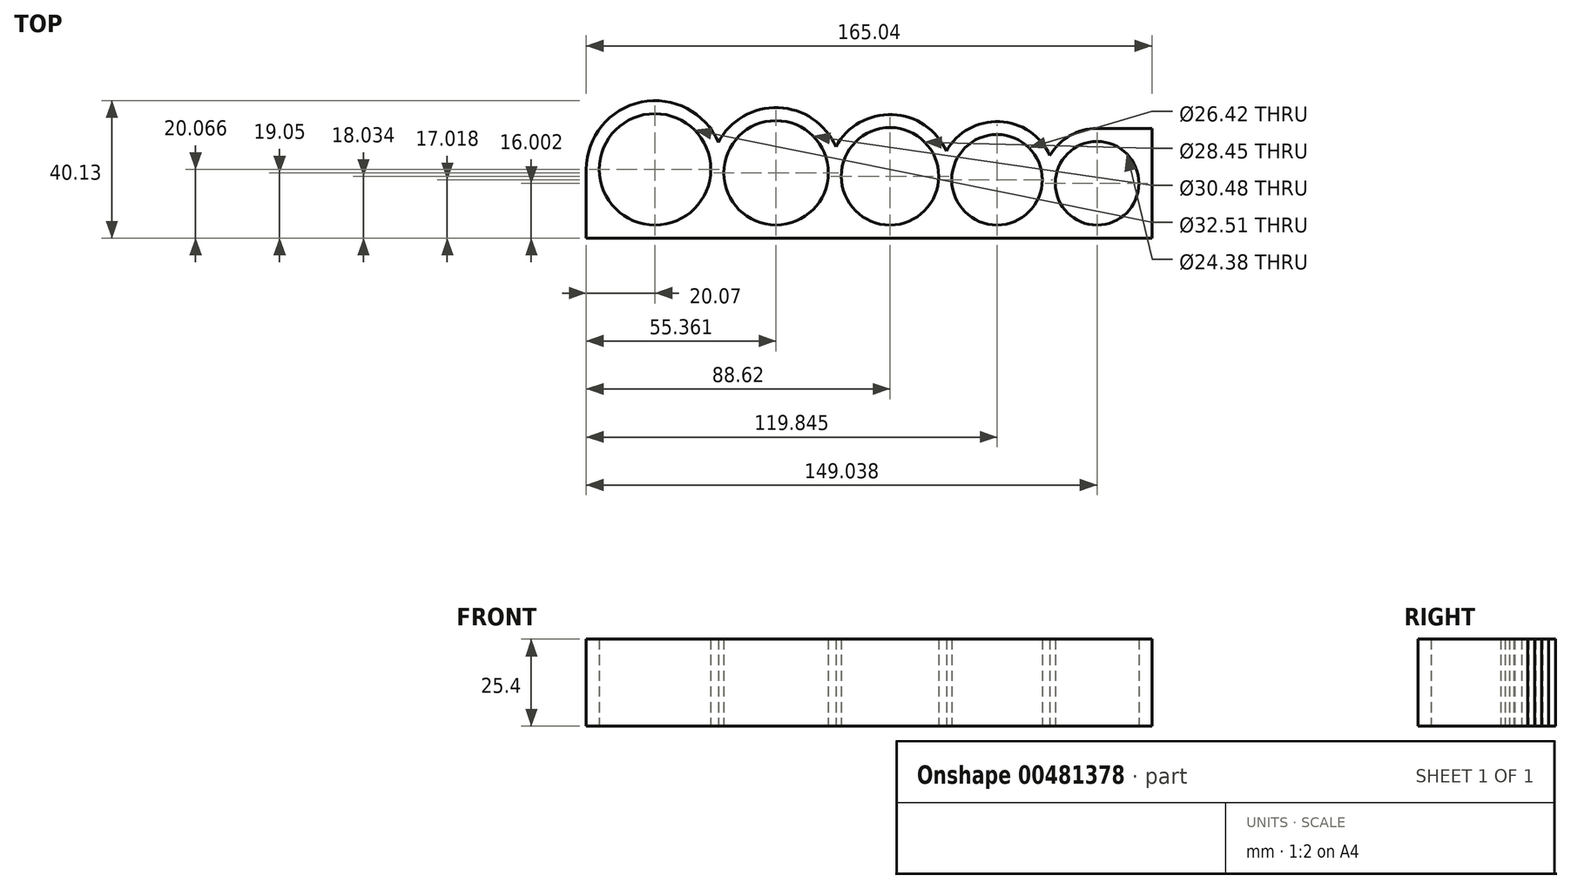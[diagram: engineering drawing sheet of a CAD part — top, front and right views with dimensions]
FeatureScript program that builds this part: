
annotation { "Feature Type Name" : "Feature", "Feature Type Description" : "" }
export const myFeature = defineFeature(function(context is Context, id is Id, definition is map)
    precondition{}
    {
        {
            var Q0;
            Q0=qCreatedBy(makeId("Top.planeOp"),FACE);
            var sketch = newSketch(context, id + "F0", { "sketchPlane" : qUnion([Q0])});
            skCircle(sketch, "E0", {"center": v(0, 20.07) * mm, "radius": 16.26 * mm});
            skCircle(sketch, "E1.0", {"center": v(0, 20.07) * mm, "radius": 20.07 * mm});
            skCircle(sketch, "E2", {"center": v(35.3, 19.05) * mm, "radius": 15.24 * mm});
            skCircle(sketch, "E3.0", {"center": v(35.3, 19.05) * mm, "radius": 19.05 * mm});
            skCircle(sketch, "E4", {"center": v(68.55, 18.03) * mm, "radius": 14.22 * mm});
            skCircle(sketch, "E5.0", {"center": v(68.55, 18.03) * mm, "radius": 18.03 * mm});
            skCircle(sketch, "E6", {"center": v(99.78, 17.02) * mm, "radius": 13.2 * mm});
            skCircle(sketch, "E7.0", {"center": v(99.78, 17.02) * mm, "radius": 17.02 * mm});
            skCircle(sketch, "E8", {"center": v(128.97, 16) * mm, "radius": 12.2 * mm});
            skCircle(sketch, "E9.0", {"center": v(128.97, 16) * mm, "radius": 16 * mm});
            skLineSegment(sketch, "E10", {"start": v(-20.07, 20.07) * mm, "end": v(-20.07, 0) * mm});
            skLineSegment(sketch, "E11", {"start": v(-20.07, 0) * mm, "end": v(144.97, 0) * mm});
            skLineSegment(sketch, "E12", {"start": v(144.97, 0) * mm, "end": v(144.97, 16) * mm});
            skLineSegment(sketch, "E13", {"start": v(128.97, 32) * mm, "end": v(144.97, 32) * mm});
            skLineSegment(sketch, "E14", {"start": v(144.97, 32) * mm, "end": v(144.97, 16) * mm});
            skSolve(sketch);
        }
        {
            var Q0;
            {var subQ0=sQuery(id+"F0.wireOp",EDGE,"E10");Q0=makeQuery(id+"F0.imprint","IMPRINT",FACE,{"disambiguationData":[TD([[makeQuery(id+"F0.imprint","IMPRINT",EDGE,{"derivedFrom":subQ0}),1.0]])]});}
            var Q1;
            {var subQ6=sQuery(id+"F0.wireOp",EDGE,"E0");Q1=makeQuery(id+"F0.imprint","IMPRINT",FACE,{"disambiguationData":[TD([[makeQuery(id+"F0.imprint","IMPRINT",EDGE,{"derivedFrom":subQ6}),-1.0]])]});}
            var Q2;
            {var subQ0=sQuery(id+"F0.wireOp",EDGE,"E3.0");var subQ1=sQuery(id+"F0.wireOp",EDGE,"E1.0");var subQ2=makeQuery(id+"F0.imprint","INTERSECT",VERTEX,{"disambiguationData":[OD(1.0)],"derivedFrom":[subQ1,subQ0]});Q2=makeQuery(id+"F0.imprint","IMPRINT",FACE,{"disambiguationData":[TD([[makeQuery(id+"F0.imprint","IMPRINT",EDGE,{"disambiguationData":[TD([[subQ2,-1.0]])],"derivedFrom":subQ1}),1.0]])]});}
            var Q3;
            {var subQ0=sQuery(id+"F0.wireOp",EDGE,"E11");var subQ1=sQuery(id+"F0.wireOp",EDGE,"E1.0");var subQ2=makeQuery(id+"F0.imprint","INTERSECT",VERTEX,{"derivedFrom":[subQ1,subQ0]});Q3=makeQuery(id+"F0.imprint","IMPRINT",FACE,{"disambiguationData":[TD([[makeQuery(id+"F0.imprint","IMPRINT",EDGE,{"disambiguationData":[TD([[subQ2,-1.0]])],"derivedFrom":subQ1}),-1.0]])]});}
            var Q4;
            {var subQ0=sQuery(id+"F0.wireOp",EDGE,"E3.0");var subQ1=sQuery(id+"F0.wireOp",EDGE,"E1.0");var subQ2=makeQuery(id+"F0.imprint","INTERSECT",VERTEX,{"disambiguationData":[OD(0.0)],"derivedFrom":[subQ1,subQ0]});Q4=makeQuery(id+"F0.imprint","IMPRINT",FACE,{"disambiguationData":[TD([[makeQuery(id+"F0.imprint","IMPRINT",EDGE,{"disambiguationData":[TD([[subQ2,1.0]])],"derivedFrom":subQ1}),-1.0]])]});}
            var Q5;
            {var subQ0=sQuery(id+"F0.wireOp",EDGE,"E3.0");var subQ4=sQuery(id+"F0.wireOp",EDGE,"E1.0");var subQ5=makeQuery(id+"F0.imprint","INTERSECT",VERTEX,{"disambiguationData":[OD(1.0)],"derivedFrom":[subQ4,subQ0]});Q5=makeQuery(id+"F0.imprint","IMPRINT",FACE,{"disambiguationData":[TD([[makeQuery(id+"F0.imprint","IMPRINT",EDGE,{"disambiguationData":[TD([[subQ5,-1.0]])],"derivedFrom":subQ4}),-1.0]])]});}
            var Q6;
            {var subQ0=sQuery(id+"F0.wireOp",EDGE,"E5.0");var subQ1=sQuery(id+"F0.wireOp",EDGE,"E3.0");var subQ2=makeQuery(id+"F0.imprint","INTERSECT",VERTEX,{"disambiguationData":[OD(1.0)],"derivedFrom":[subQ1,subQ0]});Q6=makeQuery(id+"F0.imprint","IMPRINT",FACE,{"disambiguationData":[TD([[makeQuery(id+"F0.imprint","IMPRINT",EDGE,{"disambiguationData":[TD([[subQ2,-1.0]])],"derivedFrom":subQ1}),1.0]])]});}
            var Q7;
            {var subQ0=sQuery(id+"F0.wireOp",EDGE,"E11");var subQ1=sQuery(id+"F0.wireOp",EDGE,"E3.0");var subQ2=makeQuery(id+"F0.imprint","INTERSECT",VERTEX,{"derivedFrom":[subQ1,subQ0]});Q7=makeQuery(id+"F0.imprint","IMPRINT",FACE,{"disambiguationData":[TD([[makeQuery(id+"F0.imprint","IMPRINT",EDGE,{"disambiguationData":[TD([[subQ2,-1.0]])],"derivedFrom":subQ1}),-1.0]])]});}
            var Q8;
            {var subQ0=sQuery(id+"F0.wireOp",EDGE,"E5.0");var subQ4=sQuery(id+"F0.wireOp",EDGE,"E3.0");var subQ5=makeQuery(id+"F0.imprint","INTERSECT",VERTEX,{"disambiguationData":[OD(1.0)],"derivedFrom":[subQ4,subQ0]});Q8=makeQuery(id+"F0.imprint","IMPRINT",FACE,{"disambiguationData":[TD([[makeQuery(id+"F0.imprint","IMPRINT",EDGE,{"disambiguationData":[TD([[subQ5,-1.0]])],"derivedFrom":subQ4}),-1.0]])]});}
            var Q9;
            {var subQ0=sQuery(id+"F0.wireOp",EDGE,"E7.0");var subQ1=sQuery(id+"F0.wireOp",EDGE,"E5.0");var subQ2=makeQuery(id+"F0.imprint","INTERSECT",VERTEX,{"disambiguationData":[OD(1.0)],"derivedFrom":[subQ1,subQ0]});Q9=makeQuery(id+"F0.imprint","IMPRINT",FACE,{"disambiguationData":[TD([[makeQuery(id+"F0.imprint","IMPRINT",EDGE,{"disambiguationData":[TD([[subQ2,-1.0]])],"derivedFrom":subQ1}),1.0]])]});}
            var Q10;
            {var subQ0=sQuery(id+"F0.wireOp",EDGE,"E5.0");var subQ1=sQuery(id+"F0.wireOp",EDGE,"E3.0");var subQ2=makeQuery(id+"F0.imprint","INTERSECT",VERTEX,{"disambiguationData":[OD(0.0)],"derivedFrom":[subQ1,subQ0]});Q10=makeQuery(id+"F0.imprint","IMPRINT",FACE,{"disambiguationData":[TD([[makeQuery(id+"F0.imprint","IMPRINT",EDGE,{"disambiguationData":[TD([[subQ2,1.0]])],"derivedFrom":subQ1}),-1.0]])]});}
            var Q11;
            {var subQ0=sQuery(id+"F0.wireOp",EDGE,"E11");var subQ1=sQuery(id+"F0.wireOp",EDGE,"E5.0");var subQ2=makeQuery(id+"F0.imprint","INTERSECT",VERTEX,{"derivedFrom":[subQ1,subQ0]});Q11=makeQuery(id+"F0.imprint","IMPRINT",FACE,{"disambiguationData":[TD([[makeQuery(id+"F0.imprint","IMPRINT",EDGE,{"disambiguationData":[TD([[subQ2,-1.0]])],"derivedFrom":subQ1}),-1.0]])]});}
            var Q12;
            {var subQ0=sQuery(id+"F0.wireOp",EDGE,"E7.0");var subQ4=sQuery(id+"F0.wireOp",EDGE,"E5.0");var subQ5=makeQuery(id+"F0.imprint","INTERSECT",VERTEX,{"disambiguationData":[OD(1.0)],"derivedFrom":[subQ4,subQ0]});Q12=makeQuery(id+"F0.imprint","IMPRINT",FACE,{"disambiguationData":[TD([[makeQuery(id+"F0.imprint","IMPRINT",EDGE,{"disambiguationData":[TD([[subQ5,-1.0]])],"derivedFrom":subQ4}),-1.0]])]});}
            var Q13;
            {var subQ0=sQuery(id+"F0.wireOp",EDGE,"E7.0");var subQ1=sQuery(id+"F0.wireOp",EDGE,"E5.0");var subQ2=makeQuery(id+"F0.imprint","INTERSECT",VERTEX,{"disambiguationData":[OD(0.0)],"derivedFrom":[subQ1,subQ0]});Q13=makeQuery(id+"F0.imprint","IMPRINT",FACE,{"disambiguationData":[TD([[makeQuery(id+"F0.imprint","IMPRINT",EDGE,{"disambiguationData":[TD([[subQ2,1.0]])],"derivedFrom":subQ1}),-1.0]])]});}
            var Q14;
            {var subQ0=sQuery(id+"F0.wireOp",EDGE,"E7.0");var subQ1=makeQuery(id+"F0.imprint","INTERSECT",VERTEX,{"derivedFrom":[subQ0,sQuery(id+"F0.wireOp",EDGE,"E8")]});Q14=makeQuery(id+"F0.imprint","IMPRINT",FACE,{"disambiguationData":[TD([[makeQuery(id+"F0.imprint","IMPRINT",EDGE,{"disambiguationData":[TD([[subQ1,1.0]])],"derivedFrom":subQ0}),1.0]])]});}
            var Q15;
            {var subQ3=sQuery(id+"F0.wireOp",EDGE,"E8");Q15=makeQuery(id+"F0.imprint","IMPRINT",FACE,{"disambiguationData":[TD([[makeQuery(id+"F0.imprint","IMPRINT",EDGE,{"derivedFrom":subQ3}),-1.0]])]});}
            var Q16;
            {var subQ0=sQuery(id+"F0.wireOp",EDGE,"E11");var subQ1=sQuery(id+"F0.wireOp",EDGE,"E7.0");var subQ2=makeQuery(id+"F0.imprint","INTERSECT",VERTEX,{"derivedFrom":[subQ1,subQ0]});Q16=makeQuery(id+"F0.imprint","IMPRINT",FACE,{"disambiguationData":[TD([[makeQuery(id+"F0.imprint","IMPRINT",EDGE,{"disambiguationData":[TD([[subQ2,-1.0]])],"derivedFrom":subQ1}),-1.0]])]});}
            var Q17;
            {var subQ0=sQuery(id+"F0.wireOp",EDGE,"E12");Q17=makeQuery(id+"F0.imprint","IMPRINT",FACE,{"disambiguationData":[TD([[makeQuery(id+"F0.imprint","IMPRINT",EDGE,{"derivedFrom":subQ0}),1.0]])]});}
            var Q18;
            {var subQ2=sQuery(id+"F0.wireOp",EDGE,"E13");Q18=makeQuery(id+"F0.imprint","IMPRINT",FACE,{"disambiguationData":[TD([[makeQuery(id+"F0.imprint","IMPRINT",EDGE,{"derivedFrom":subQ2}),-1.0]])]});}
            extrude(context, id + "F1", {"entities" : qUnion([Q0, Q1, Q2, Q3, Q4, Q5, Q6, Q7, Q8, Q9, Q10, Q11, Q12, Q13, Q14, Q15, Q16, Q17, Q18]), "depth" : 25.4 * mm});
        }
    });
